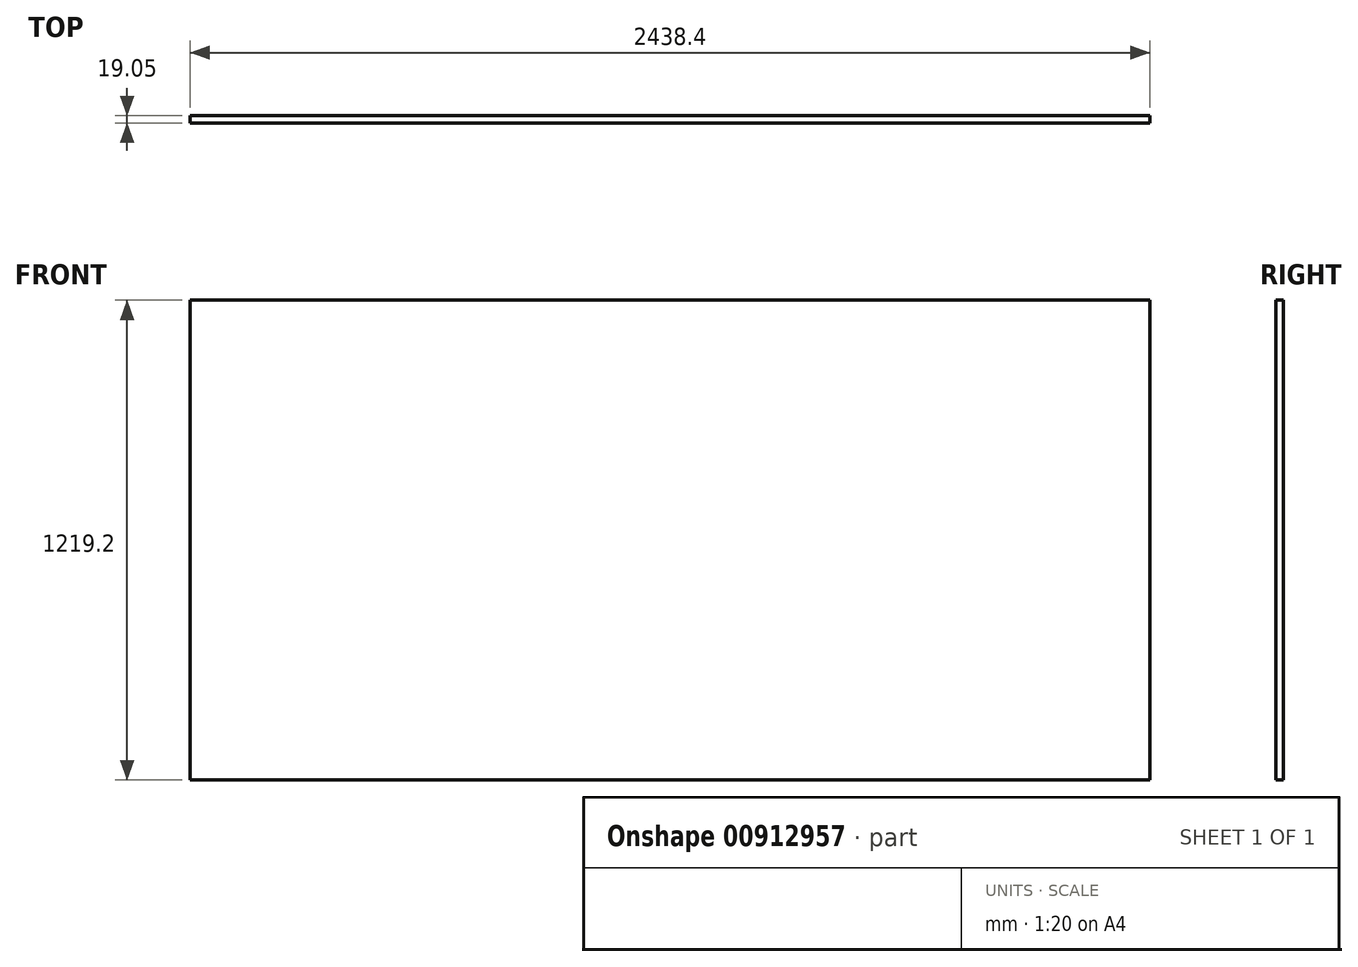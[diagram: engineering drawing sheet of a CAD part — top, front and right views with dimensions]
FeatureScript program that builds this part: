
annotation { "Feature Type Name" : "Feature", "Feature Type Description" : "" }
export const myFeature = defineFeature(function(context is Context, id is Id, definition is map)
    precondition{}
    {
        {
            var Q0;
            Q0=qCreatedBy(makeId("Front.planeOp"),FACE);
            var sketch = newSketch(context, id + "F0", { "sketchPlane" : qUnion([Q0]), "asVersion" : FeatureScriptVersionNumber.V729_UPGRADE_FIXES});
            skLineSegment(sketch, "E0.bottom", {"start": v(1219.2, -609.6) * mm, "end": v(-1219.2, -609.6) * mm});
            skLineSegment(sketch, "E0.top", {"start": v(1219.2, 609.6) * mm, "end": v(-1219.2, 609.6) * mm});
            skLineSegment(sketch, "E0.left", {"start": v(1219.2, -609.6) * mm, "end": v(1219.2, 609.6) * mm});
            skLineSegment(sketch, "E0.right", {"start": v(-1219.2, -609.6) * mm, "end": v(-1219.2, 609.6) * mm});
            skPoint(sketch, "E0.middle", {"position": v(0, 0) * mm});
            skSolve(sketch);
        }
        {
            var Q0;
            Q0=makeQuery(id+"F0.imprint","IMPRINT",FACE,{"disambiguationData":[TD([[makeQuery(id+"F0.imprint","IMPRINT",EDGE,{"derivedFrom":sQuery(id+"F0.wireOp",EDGE,"E0.bottom")}),-1.0]])]});
            var sketch = newSketch(context, id + "F1", { "sketchPlane" : qUnion([Q0]), "asVersion" : FeatureScriptVersionNumber.V729_UPGRADE_FIXES});
            skSolve(sketch);
        }
        {
            var Q0;
            Q0=makeQuery(id+"F1.imprint","IMPRINT",FACE,{"disambiguationData":[TD([[makeQuery(id+"F1.imprint","IMPRINT",EDGE,{"derivedFrom":makeQuery(id+"F0.imprint","IMPRINT",EDGE,{"derivedFrom":sQuery(id+"F0.wireOp",EDGE,"E0.bottom")})}),-1.0]])]});
            extrude(context, id + "F2", {"entities" : qUnion([Q0]), "depth" : 19.05 * mm, "offsetDistance" : 25.4 * mm});
        }
    });
